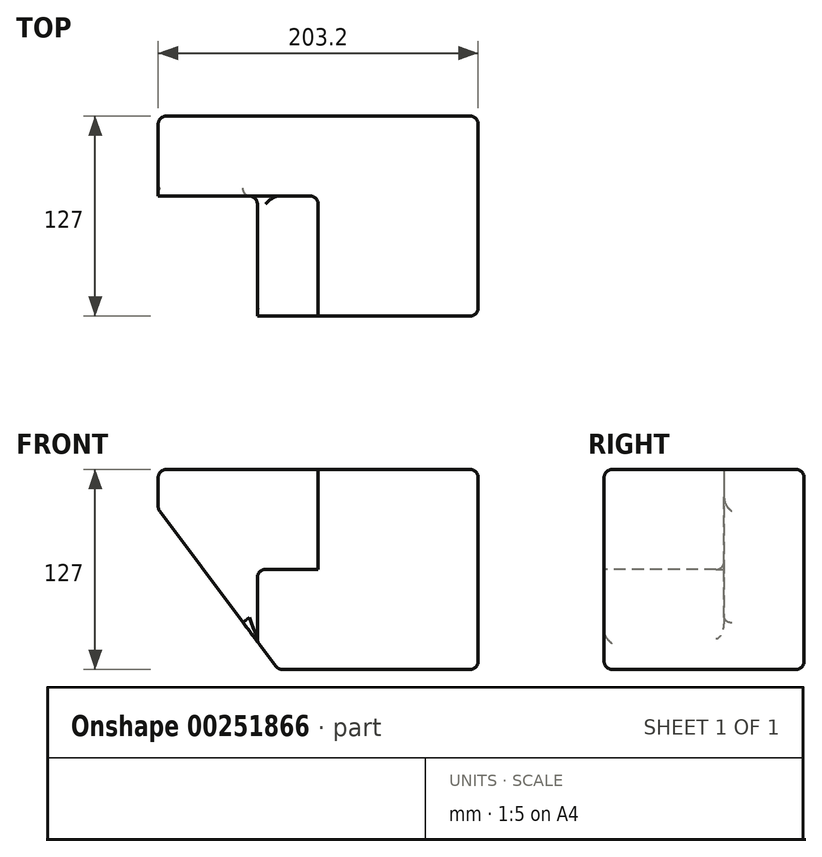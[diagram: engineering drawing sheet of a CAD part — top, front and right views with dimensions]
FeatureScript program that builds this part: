
annotation { "Feature Type Name" : "Feature", "Feature Type Description" : "" }
export const myFeature = defineFeature(function(context is Context, id is Id, definition is map)
    precondition{}
    {
        {
            var Q0;
            Q0=qCreatedBy(makeId("Front.planeOp"),FACE);
            var sketch = newSketch(context, id + "F0", { "sketchPlane" : qUnion([Q0])});
            skLineSegment(sketch, "E0.bottom", {"start": v(-49.44, 50.87) * mm, "end": v(153.76, 50.87) * mm});
            skLineSegment(sketch, "E0.top", {"start": v(-49.44, -76.13) * mm, "end": v(153.76, -76.13) * mm});
            skLineSegment(sketch, "E0.left", {"start": v(-49.44, 50.87) * mm, "end": v(-49.44, -76.13) * mm});
            skLineSegment(sketch, "E0.right", {"start": v(153.76, 50.87) * mm, "end": v(153.76, -76.13) * mm});
            skSolve(sketch);
        }
        {
            var Q0;
            Q0=makeQuery(id+"F0.imprint","IMPRINT",FACE,{"disambiguationData":[TD([[makeQuery(id+"F0.imprint","IMPRINT",EDGE,{"derivedFrom":sQuery(id+"F0.wireOp",EDGE,"E0.bottom")}),-1.0]])]});
            extrude(context, id + "F1", {"entities" : qUnion([Q0]), "depth" : 127 * mm});
        }
        {
            var Q0;
            Q0=makeQuery(id+"F1.opExtrude","CAP_FACE",FACE,{"disambiguationData":[OSD([sQuery(id+"F0.wireOp",EDGE,"E0.bottom"),sQuery(id+"F0.wireOp",EDGE,"E0.top"),sQuery(id+"F0.wireOp",EDGE,"E0.left"),sQuery(id+"F0.wireOp",EDGE,"E0.right")])],"isStart":false});
            var sketch = newSketch(context, id + "F2", { "sketchPlane" : qUnion([Q0])});
            skLineSegment(sketch, "E1", {"start": v(-49.44, 50.87) * mm, "end": v(52.16, 50.87) * mm});
            skLineSegment(sketch, "E2", {"start": v(52.16, 50.87) * mm, "end": v(52.16, -12.63) * mm});
            skLineSegment(sketch, "E3", {"start": v(52.16, -12.63) * mm, "end": v(13.5, -12.63) * mm});
            skLineSegment(sketch, "E4", {"start": v(13.5, -12.63) * mm, "end": v(13.5, -76.13) * mm});
            skLineSegment(sketch, "E5", {"start": v(13.5, -76.13) * mm, "end": v(-49.44, -76.13) * mm});
            skLineSegment(sketch, "E6", {"start": v(-49.44, -76.13) * mm, "end": v(-49.44, 50.87) * mm});
            skSolve(sketch);
        }
        {
            var Q0;
            Q0=makeQuery(id+"F2.imprint","IMPRINT",FACE,{"disambiguationData":[TD([[makeQuery(id+"F2.imprint","IMPRINT",EDGE,{"derivedFrom":sQuery(id+"F2.wireOp",EDGE,"E1")}),-1.0]])]});
            extrude(context, id + "F3", {"entities" : qUnion([Q0]), "operationType" : NewBodyOperationType.REMOVE, "oppositeDirection" : true, "depth" : 76.2 * mm});
        }
        {
            var Q0;
            Q0=makeQuery(id+"F1.opExtrude","SWEPT_EDGE",EDGE,{"disambiguationData":[OSD([sQuery(id+"F0.wireOp",EDGE,"E0.top"),sQuery(id+"F0.wireOp",EDGE,"E0.left")])]});
            chamfer(context, id + "F4", {"entities" : qUnion([Q0]), "chamferType" : ChamferType.TWO_OFFSETS, "width1" : 76.2 * mm, "oppositeDirection" : false, "width2" : 101.6 * mm});
        }
        {
            var Q0;
            Q0=makeQuery(id+"F3.boolean.opBoolean","COPY",EDGE,{"derivedFrom":makeQuery(id+"F3.opExtrude","CAP_EDGE",EDGE,{"disambiguationData":[OSD([sQuery(id+"F2.wireOp",EDGE,"E4")])],"isStart":true})});
            var Q1;
            Q1=makeQuery(id+"F3.boolean.opBoolean","COPY",EDGE,{"derivedFrom":makeQuery(id+"F3.opExtrude","SWEPT_EDGE",EDGE,{"disambiguationData":[OSD([sQuery(id+"F2.wireOp",EDGE,"E3"),sQuery(id+"F2.wireOp",EDGE,"E4")])]})});
            var Q2;
            Q2=makeQuery(id+"F3.boolean.opBoolean","COPY",EDGE,{"derivedFrom":makeQuery(id+"F3.opExtrude","CAP_EDGE",EDGE,{"disambiguationData":[OSD([sQuery(id+"F2.wireOp",EDGE,"E4")])],"isStart":false})});
            var Q3;
            Q3=makeQuery(id+"F3.boolean.opBoolean","COPY",EDGE,{"derivedFrom":makeQuery(id+"F3.opExtrude","CAP_EDGE",EDGE,{"disambiguationData":[OSD([sQuery(id+"F2.wireOp",EDGE,"E2")])],"isStart":false})});
            var Q4;
            Q4=makeQuery(id+"F3.boolean.opBoolean","COPY",EDGE,{"derivedFrom":makeQuery(id+"F3.opExtrude","CAP_EDGE",EDGE,{"disambiguationData":[OSD([sQuery(id+"F2.wireOp",EDGE,"E1")])],"isStart":false})});
            var Q5;
            Q5=makeQuery(id+"F1.opExtrude","SWEPT_EDGE",EDGE,{"disambiguationData":[OSD([sQuery(id+"F0.wireOp",EDGE,"E0.bottom"),sQuery(id+"F0.wireOp",EDGE,"E0.left")])]});
            var Q6;
            Q6=makeQuery(id+"F1.opExtrude","CAP_EDGE",EDGE,{"disambiguationData":[OSD([sQuery(id+"F0.wireOp",EDGE,"E0.left")])],"isStart":true});
            var Q7;
            Q7=makeQuery(id+"F1.opExtrude","CAP_EDGE",EDGE,{"disambiguationData":[OSD([sQuery(id+"F0.wireOp",EDGE,"E0.top")])],"isStart":false});
            var Q8;
            Q8=makeQuery(id+"F1.opExtrude","SWEPT_EDGE",EDGE,{"disambiguationData":[OSD([sQuery(id+"F0.wireOp",EDGE,"E0.top"),sQuery(id+"F0.wireOp",EDGE,"E0.right")])]});
            var Q9;
            Q9=makeQuery(id+"F1.opExtrude","CAP_EDGE",EDGE,{"disambiguationData":[OSD([sQuery(id+"F0.wireOp",EDGE,"E0.top")])],"isStart":true});
            var Q10;
            Q10=makeQuery(id+"F1.opExtrude","CAP_EDGE",EDGE,{"disambiguationData":[OSD([sQuery(id+"F0.wireOp",EDGE,"E0.right")])],"isStart":false});
            var Q11;
            Q11=makeQuery(id+"F1.opExtrude","CAP_EDGE",EDGE,{"disambiguationData":[OSD([sQuery(id+"F0.wireOp",EDGE,"E0.bottom")])],"isStart":false});
            var Q12;
            Q12=makeQuery(id+"F3.boolean.opBoolean","COPY",EDGE,{"derivedFrom":makeQuery(id+"F3.opExtrude","CAP_EDGE",EDGE,{"disambiguationData":[OSD([sQuery(id+"F2.wireOp",EDGE,"E2")])],"isStart":true})});
            var Q13;
            Q13=makeQuery(id+"F3.boolean.opBoolean","COPY",EDGE,{"derivedFrom":makeQuery(id+"F3.opExtrude","CAP_EDGE",EDGE,{"disambiguationData":[OSD([sQuery(id+"F2.wireOp",EDGE,"E3")])],"isStart":true})});
            var Q14;
            Q14=makeQuery(id+"F1.opExtrude","SWEPT_EDGE",EDGE,{"disambiguationData":[OSD([sQuery(id+"F0.wireOp",EDGE,"E0.bottom"),sQuery(id+"F0.wireOp",EDGE,"E0.right")])]});
            var Q15;
            Q15=makeQuery(id+"F1.opExtrude","CAP_EDGE",EDGE,{"disambiguationData":[OSD([sQuery(id+"F0.wireOp",EDGE,"E0.bottom")])],"isStart":true});
            var Q16;
            Q16=makeQuery(id+"F1.opExtrude","CAP_EDGE",EDGE,{"disambiguationData":[OSD([sQuery(id+"F0.wireOp",EDGE,"E0.right")])],"isStart":true});
            var Q17;
            Q17=makeQuery(id+"F3.boolean.opBoolean","COPY",EDGE,{"derivedFrom":makeQuery(id+"F3.opExtrude","CAP_EDGE",EDGE,{"disambiguationData":[OSD([sQuery(id+"F2.wireOp",EDGE,"E6")])],"isStart":false})});
            var Q18;
            Q18=makeQuery(id+"F4.opChamfer","BLEND_FACE",FACE,{"disambiguationData":[OSD([sQuery(id+"F0.wireOp",EDGE,"E0.top"),sQuery(id+"F0.wireOp",EDGE,"E0.left")])]});
            var Q19;
            Q19=makeQuery(id+"F4.opChamfer","BLEND_EDGE",EDGE,{"blendedFrom":[makeQuery(id+"F1.opExtrude","SWEPT_EDGE",EDGE,{"disambiguationData":[OSD([sQuery(id+"F0.wireOp",EDGE,"E0.top"),sQuery(id+"F0.wireOp",EDGE,"E0.left")])]}),makeQuery(id+"F3.boolean.opBoolean","COPY",FACE,{"derivedFrom":makeQuery(id+"F3.opExtrude","CAP_FACE",FACE,{"disambiguationData":[OSD([sQuery(id+"F2.wireOp",EDGE,"E1"),sQuery(id+"F2.wireOp",EDGE,"E2"),sQuery(id+"F2.wireOp",EDGE,"E3"),sQuery(id+"F2.wireOp",EDGE,"E4"),sQuery(id+"F2.wireOp",EDGE,"E5"),sQuery(id+"F2.wireOp",EDGE,"E6")])],"isStart":false})})],"blendedInto":[makeQuery(id+"F3.boolean.opBoolean","COPY",FACE,{"derivedFrom":makeQuery(id+"F3.opExtrude","CAP_FACE",FACE,{"disambiguationData":[OSD([sQuery(id+"F2.wireOp",EDGE,"E1"),sQuery(id+"F2.wireOp",EDGE,"E2"),sQuery(id+"F2.wireOp",EDGE,"E3"),sQuery(id+"F2.wireOp",EDGE,"E4"),sQuery(id+"F2.wireOp",EDGE,"E5"),sQuery(id+"F2.wireOp",EDGE,"E6")])],"isStart":false})})]});
            var Q20;
            {var subQ0=sQuery(id+"F0.wireOp",EDGE,"E0.left");var subQ1=sQuery(id+"F0.wireOp",EDGE,"E0.top");Q20=makeQuery(id+"F4.opChamfer","BLEND_EDGE",EDGE,{"blendedFrom":[makeQuery(id+"F1.opExtrude","SWEPT_EDGE",EDGE,{"disambiguationData":[OSD([subQ1,subQ0])]}),makeQuery(id+"F1.opExtrude","CAP_FACE",FACE,{"disambiguationData":[OSD([sQuery(id+"F0.wireOp",EDGE,"E0.bottom"),subQ1,subQ0,sQuery(id+"F0.wireOp",EDGE,"E0.right")])],"isStart":true})],"blendedInto":[makeQuery(id+"F1.opExtrude","CAP_FACE",FACE,{"disambiguationData":[OSD([sQuery(id+"F0.wireOp",EDGE,"E0.bottom"),subQ1,subQ0,sQuery(id+"F0.wireOp",EDGE,"E0.right")])],"isStart":true})]});}
            var Q21;
            {var subQ0=sQuery(id+"F0.wireOp",EDGE,"E0.left");Q21=makeQuery(id+"F4.opChamfer","BLEND_EDGE",EDGE,{"blendedFrom":[makeQuery(id+"F1.opExtrude","SWEPT_EDGE",EDGE,{"disambiguationData":[OSD([sQuery(id+"F0.wireOp",EDGE,"E0.top"),subQ0])]}),makeQuery(id+"F1.opExtrude","SWEPT_FACE",FACE,{"disambiguationData":[OSD([subQ0])]})],"blendedInto":[makeQuery(id+"F1.opExtrude","SWEPT_FACE",FACE,{"disambiguationData":[OSD([subQ0])]})]});}
            var Q22;
            Q22=makeQuery(id+"F4.opChamfer","BLEND_EDGE",EDGE,{"blendedFrom":[makeQuery(id+"F1.opExtrude","SWEPT_EDGE",EDGE,{"disambiguationData":[OSD([sQuery(id+"F0.wireOp",EDGE,"E0.top"),sQuery(id+"F0.wireOp",EDGE,"E0.left")])]}),makeQuery(id+"F3.boolean.opBoolean","COPY",FACE,{"derivedFrom":makeQuery(id+"F3.opExtrude","SWEPT_FACE",FACE,{"disambiguationData":[OSD([sQuery(id+"F2.wireOp",EDGE,"E4")])]})})],"blendedInto":[makeQuery(id+"F3.boolean.opBoolean","COPY",FACE,{"derivedFrom":makeQuery(id+"F3.opExtrude","SWEPT_FACE",FACE,{"disambiguationData":[OSD([sQuery(id+"F2.wireOp",EDGE,"E4")])]})})]});
            fillet(context, id + "F5", {"entities" : qUnion([Q0, Q1, Q2, Q3, Q4, Q5, Q6, Q7, Q8, Q9, Q10, Q11, Q12, Q13, Q14, Q15, Q16, Q17, Q18, Q19, Q20, Q21, Q22]), "radius" : 5.08 * mm, "tangentPropagation" : true, "allowEdgeOverflow" : false});
        }
    });
